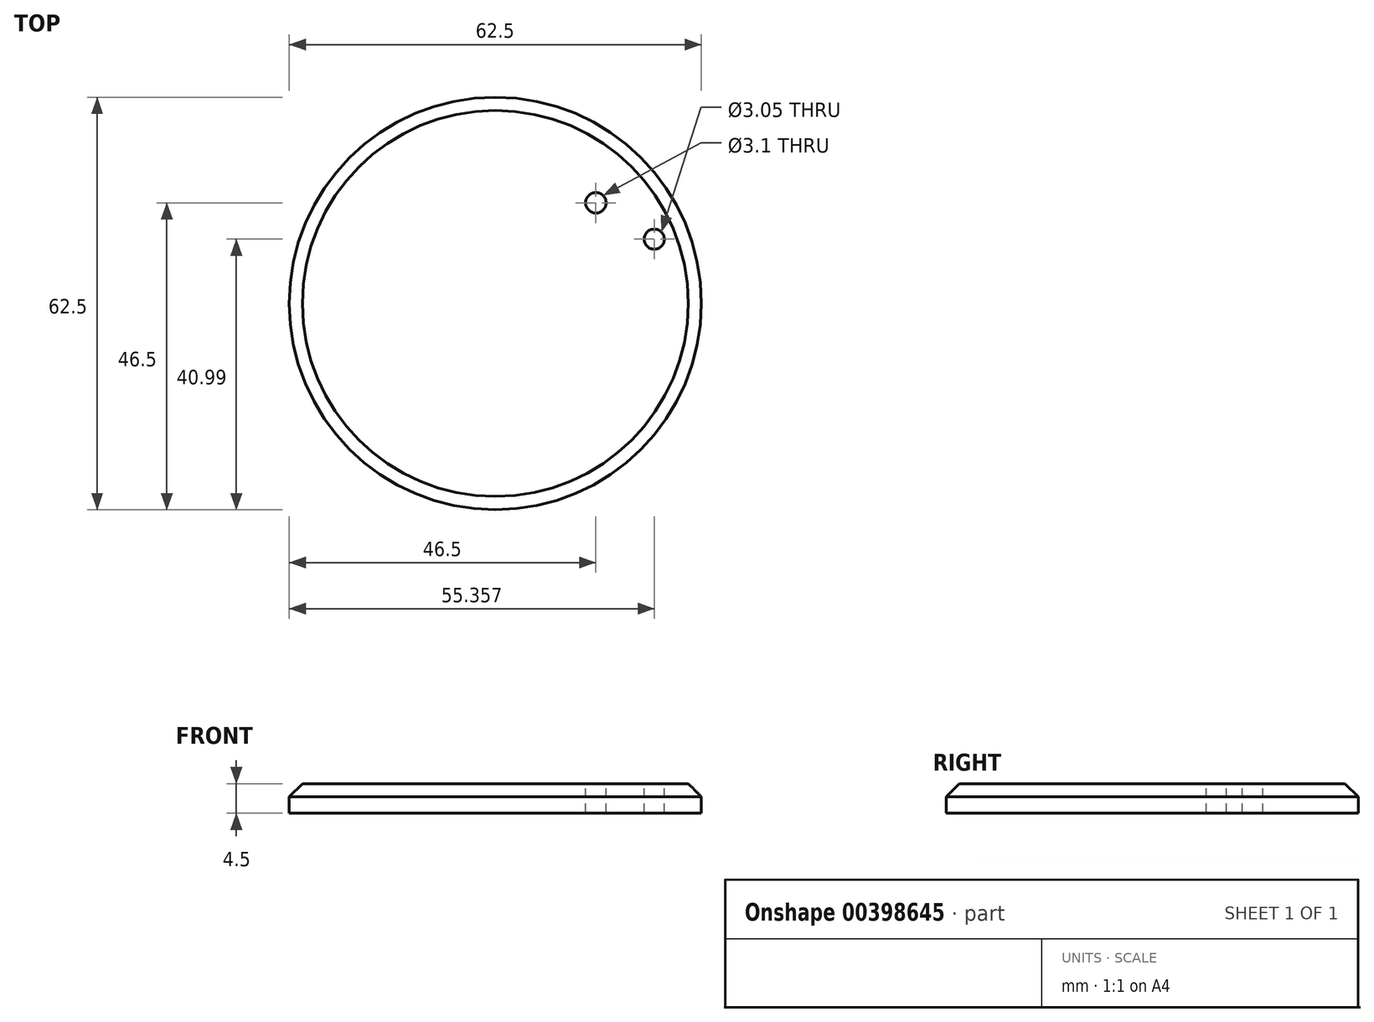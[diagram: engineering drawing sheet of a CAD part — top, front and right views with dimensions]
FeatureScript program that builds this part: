
annotation { "Feature Type Name" : "Feature", "Feature Type Description" : "" }
export const myFeature = defineFeature(function(context is Context, id is Id, definition is map)
    precondition{}
    {
        {
            var Q0;
            Q0=qCreatedBy(makeId("Top.planeOp"),FACE);
            var sketch = newSketch(context, id + "F0", { "sketchPlane" : qUnion([Q0])});
            skCircle(sketch, "E0", {"center": v(0, 0) * mm, "radius": 31.25 * mm});
            skSolve(sketch);
        }
        {
            var Q0;
            Q0=makeQuery(id+"F0.imprint","IMPRINT",FACE,{"disambiguationData":[TD([[makeQuery(id+"F0.imprint","IMPRINT",EDGE,{"derivedFrom":sQuery(id+"F0.wireOp",EDGE,"E0")}),1.0]])]});
            extrude(context, id + "F1", {"entities" : qUnion([Q0]), "depth" : 4.5 * mm});
        }
        {
            var Q0;
            Q0=makeQuery(id+"F1.opExtrude","CAP_FACE",FACE,{"disambiguationData":[OSD([sQuery(id+"F0.wireOp",EDGE,"E0")])],"isStart":false});
            var sketch = newSketch(context, id + "F2", { "sketchPlane" : qUnion([Q0])});
            skLineSegment(sketch, "E1", {"start": v(0, 0) * mm, "end": v(24.1, 9.74) * mm, "construction": true});
            skLineSegment(sketch, "E2", {"start": v(0, 0) * mm, "end": v(0, 26) * mm, "construction": true});
            skCircle(sketch, "E3", {"center": v(24.1, 9.74) * mm, "radius": 1.52 * mm});
            skCircle(sketch, "E4", {"center": v(0, 0) * mm, "radius": 26 * mm, "construction": true});
            skSolve(sketch);
        }
        {
            var Q0;
            Q0 = qSketchRegion(id + "F2", true);
            extrude(context, id + "F3", {"entities" : qUnion([Q0]), "operationType" : NewBodyOperationType.REMOVE, "endBound" : BoundingType.THROUGH_ALL, "oppositeDirection" : true, "depth" : 25 * mm});
        }
        {
            var Q0;
            Q0=makeQuery(id+"F1.opExtrude","CAP_EDGE",EDGE,{"disambiguationData":[OSD([sQuery(id+"F0.wireOp",EDGE,"E0")])],"isStart":false});
            chamfer(context, id + "F4", {"entities" : qUnion([Q0]), "width" : 2 * mm, "tangentPropagation" : true});
        }
        {
            var Q0;
            Q0=makeQuery(id+"F1.opExtrude","CAP_FACE",FACE,{"disambiguationData":[OSD([sQuery(id+"F0.wireOp",EDGE,"E0")])],"isStart":false});
            var sketch = newSketch(context, id + "F5", { "sketchPlane" : qUnion([Q0])});
            skLineSegment(sketch, "E5.bottom", {"start": v(15.25, -15.25) * mm, "end": v(-15.25, -15.25) * mm, "construction": true});
            skLineSegment(sketch, "E5.top", {"start": v(15.25, 15.25) * mm, "end": v(-15.25, 15.25) * mm, "construction": true});
            skLineSegment(sketch, "E5.left", {"start": v(15.25, -15.25) * mm, "end": v(15.25, 15.25) * mm, "construction": true});
            skLineSegment(sketch, "E5.right", {"start": v(-15.25, -15.25) * mm, "end": v(-15.25, 15.25) * mm, "construction": true});
            skPoint(sketch, "E5.middle", {"position": v(0, 0) * mm});
            skCircle(sketch, "E6", {"center": v(15.25, 15.25) * mm, "radius": 1.55 * mm});
            skSolve(sketch);
        }
        {
            var Q0;
            Q0 = qSketchRegion(id + "F5", true);
            extrude(context, id + "F6", {"entities" : qUnion([Q0]), "operationType" : NewBodyOperationType.REMOVE, "endBound" : BoundingType.THROUGH_ALL, "oppositeDirection" : true, "depth" : 25 * mm});
        }
    });
